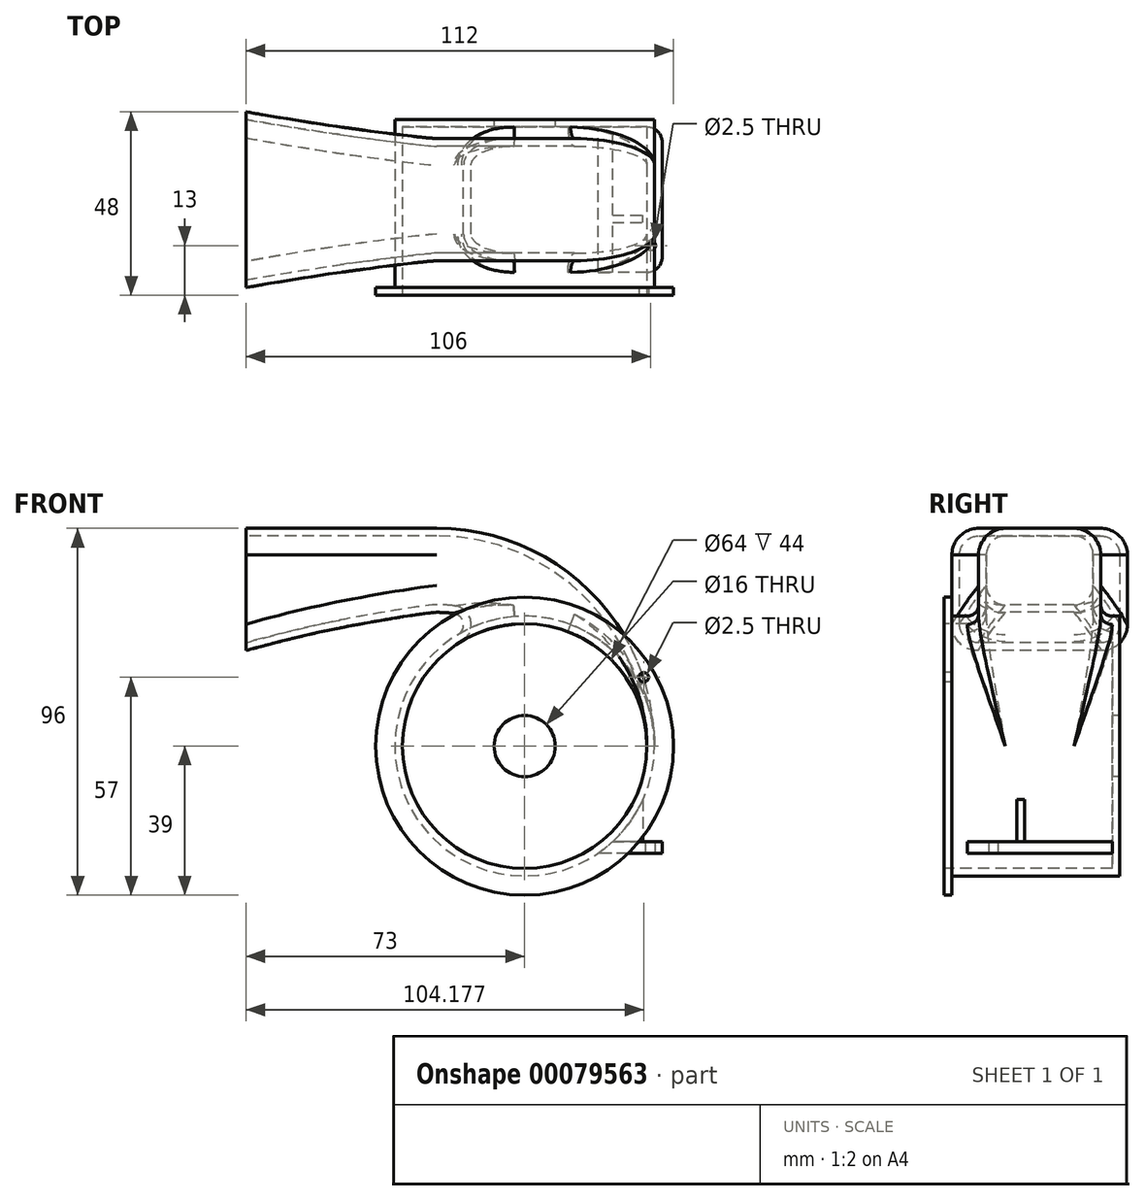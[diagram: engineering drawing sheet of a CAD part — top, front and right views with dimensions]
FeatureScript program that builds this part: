
annotation { "Feature Type Name" : "Feature", "Feature Type Description" : "" }
export const myFeature = defineFeature(function(context is Context, id is Id, definition is map)
    precondition{}
    {
        {
            var Q0;
            Q0=qCreatedBy(makeId("Front.planeOp"),FACE);
            var sketch = newSketch(context, id + "F0", { "sketchPlane" : qUnion([Q0])});
            skCircle(sketch, "E0", {"center": v(0, 0) * mm, "radius": 34 * mm});
            skSolve(sketch);
        }
        {
            var Q0;
            Q0=makeQuery(id+"F0.imprint","IMPRINT",FACE,{"disambiguationData":[TD([[makeQuery(id+"F0.imprint","IMPRINT",EDGE,{"derivedFrom":sQuery(id+"F0.wireOp",EDGE,"E0")}),1.0]])]});
            extrude(context, id + "F1", {"entities" : qUnion([Q0]), "oppositeDirection" : true, "depth" : 21 * mm, "hasSecondDirection" : true, "secondDirectionOppositeDirection" : false, "secondDirectionDepth" : 23 * mm});
        }
        {
            var Q0;
            Q0=qCreatedBy(makeId("Top.planeOp"),FACE);
            var sketch = newSketch(context, id + "F2", { "sketchPlane" : qUnion([Q0])});
            skLineSegment(sketch, "E1", {"start": v(34, 21) * mm, "end": v(34, -23) * mm});
            skLineSegment(sketch, "E2", {"start": v(-23, 15.54) * mm, "end": v(-23, -11.93) * mm, "construction": true});
            skLineSegment(sketch, "E3.bottom", {"start": v(34, 16) * mm, "end": v(12, 16) * mm});
            skLineSegment(sketch, "E3.top", {"start": v(34, -16) * mm, "end": v(12, -16) * mm});
            skLineSegment(sketch, "E3.left", {"start": v(34, 16) * mm, "end": v(34, -16) * mm});
            skLineSegment(sketch, "E3.right", {"start": v(12, 16) * mm, "end": v(12, -16) * mm});
            skPoint(sketch, "E3.middle", {"position": v(23, 0) * mm});
            skSolve(sketch);
        }
        {
            var Q0;
            Q0 = qSketchRegion(id + "F2", true);
            var Q1;
            Q1=sQuery(id+"F2.wireOp",EDGE,"E2");
            revolve(context, id + "F3", {"operationType" : NewBodyOperationType.ADD, "entities" : qUnion([Q0]), "axis" : qUnion([Q1]), "revolveType" : RevolveType.ONE_DIRECTION, "angle" : 90 * degree});
        }
        {
            var Q0;
            Q0=makeQuery(id+"F3.opRevolve","CAP_FACE",FACE,{"disambiguationData":[OSD([sQuery(id+"F2.wireOp",EDGE,"E3.bottom"),sQuery(id+"F2.wireOp",EDGE,"E3.top"),sQuery(id+"F2.wireOp",EDGE,"E3.left"),sQuery(id+"F2.wireOp",EDGE,"E3.right")])],"isStart":false});
            cPlane(context, id + "F4", {"entities" : qUnion([Q0]), "cplaneType" : CPlaneType.OFFSET, "offset" : 25 * mm, "width" : 150 * mm, "height" : 150 * mm});
        }
        {
            var Q0;
            Q0=qCreatedBy(id+"F4.planeOp",FACE);
            var sketch = newSketch(context, id + "F5", { "sketchPlane" : qUnion([Q0])});
            skLineSegment(sketch, "E4", {"start": v(-19, 57) * mm, "end": v(19, 57) * mm});
            skLineSegment(sketch, "E5", {"start": v(-19, 57) * mm, "end": v(-19, 31) * mm});
            skLineSegment(sketch, "E6", {"start": v(19, 57) * mm, "end": v(19, 31) * mm});
            skLineSegment(sketch, "E7", {"start": v(-19, 31) * mm, "end": v(19, 31) * mm});
            skSolve(sketch);
        }
        {
            var Q0;
            Q0=qCreatedBy(id+"F4.planeOp",FACE);
            cPlane(context, id + "F6", {"entities" : qUnion([Q0]), "cplaneType" : CPlaneType.OFFSET, "offset" : 25 * mm, "width" : 150 * mm, "height" : 150 * mm});
        }
        {
            var Q0;
            Q0=qCreatedBy(id+"F6.planeOp",FACE);
            var sketch = newSketch(context, id + "F7", { "sketchPlane" : qUnion([Q0])});
            skLineSegment(sketch, "E8.bottom", {"start": v(-23, 57) * mm, "end": v(23, 57) * mm});
            skLineSegment(sketch, "E8.top", {"start": v(-23, 25) * mm, "end": v(23, 25) * mm});
            skLineSegment(sketch, "E8.left", {"start": v(-23, 57) * mm, "end": v(-23, 25) * mm});
            skLineSegment(sketch, "E8.right", {"start": v(23, 57) * mm, "end": v(23, 25) * mm});
            skSolve(sketch);
        }
        {
            var Q1;
            Q1=makeQuery(id+"F3.opRevolve","CAP_FACE",FACE,{"disambiguationData":[OSD([sQuery(id+"F2.wireOp",EDGE,"E3.bottom"),sQuery(id+"F2.wireOp",EDGE,"E3.top"),sQuery(id+"F2.wireOp",EDGE,"E3.left"),sQuery(id+"F2.wireOp",EDGE,"E3.right")])],"isStart":false});
            var Q2;
            Q2=makeQuery(id+"F5.imprint","IMPRINT",FACE,{"disambiguationData":[TD([[makeQuery(id+"F5.imprint","IMPRINT",EDGE,{"derivedFrom":sQuery(id+"F5.wireOp",EDGE,"E4")}),-1.0]])]});
            var Q3;
            Q3=makeQuery(id+"F7.imprint","IMPRINT",FACE,{"disambiguationData":[TD([[makeQuery(id+"F7.imprint","IMPRINT",EDGE,{"derivedFrom":sQuery(id+"F7.wireOp",EDGE,"E8.bottom")}),-1.0]])]});
            var Q4;
            Q4=sQuery(id+"F5.wireOp",EDGE,"E7");
            var Q5;
            Q5=sQuery(id+"F5.wireOp",EDGE,"E5");
            var Q6;
            Q6=sQuery(id+"F5.wireOp",EDGE,"E4");
            var Q7;
            Q7=sQuery(id+"F5.wireOp",EDGE,"E6");
            loft(context, id + "F8", {"operationType" : NewBodyOperationType.ADD, "startCondition" : LoftEndDerivativeType.MATCH_TANGENT, "startMagnitude" : .25, "sheetProfilesArray" : [{ "sheetProfileEntities" : qUnion([Q1]) }, { "sheetProfileEntities" : qUnion([Q2]) }, { "sheetProfileEntities" : qUnion([Q3]) }], "guidesArray" : [{ "guideEntities" : qUnion([Q4]), "guideDerivativeType" : LoftGuideDerivativeType.DEFAULT, "guideDerivativeMagnitude" : 1 }, { "guideEntities" : qUnion([Q5]), "guideDerivativeType" : LoftGuideDerivativeType.DEFAULT, "guideDerivativeMagnitude" : 1 }, { "guideEntities" : qUnion([Q6]), "guideDerivativeType" : LoftGuideDerivativeType.DEFAULT, "guideDerivativeMagnitude" : 1 }, { "guideEntities" : qUnion([Q7]), "guideDerivativeType" : LoftGuideDerivativeType.DEFAULT, "guideDerivativeMagnitude" : 1 }]});
        }
        {
            var Q0;
            Q0=makeQuery(id+"F8.opLoft","SWEPT_EDGE",EDGE,{"disambiguationData":[OSD([sQuery(id+"F2.wireOp",EDGE,"E3.bottom"),sQuery(id+"F2.wireOp",EDGE,"E3.right"),sQuery(id+"F5.wireOp",EDGE,"E5"),sQuery(id+"F5.wireOp",EDGE,"E7")])]});
            var Q1;
            Q1=makeQuery(id+"F8.opLoft","SWEPT_EDGE",EDGE,{"disambiguationData":[OSD([sQuery(id+"F2.wireOp",EDGE,"E3.bottom"),sQuery(id+"F2.wireOp",EDGE,"E3.left"),sQuery(id+"F5.wireOp",EDGE,"E4"),sQuery(id+"F5.wireOp",EDGE,"E5")])]});
            var Q2;
            Q2=makeQuery(id+"F8.opLoft","SWEPT_EDGE",EDGE,{"disambiguationData":[OSD([sQuery(id+"F2.wireOp",EDGE,"E3.top"),sQuery(id+"F2.wireOp",EDGE,"E3.left"),sQuery(id+"F5.wireOp",EDGE,"E4"),sQuery(id+"F5.wireOp",EDGE,"E6")])]});
            var Q3;
            Q3=makeQuery(id+"F8.opLoft","SWEPT_EDGE",EDGE,{"disambiguationData":[OSD([sQuery(id+"F2.wireOp",EDGE,"E3.top"),sQuery(id+"F2.wireOp",EDGE,"E3.right"),sQuery(id+"F5.wireOp",EDGE,"E6"),sQuery(id+"F5.wireOp",EDGE,"E7")])]});
            fillet(context, id + "F9", {"entities" : qUnion([Q0, Q1, Q2, Q3]), "radius" : 7 * mm, "tangentPropagation" : true, "allowEdgeOverflow" : false});
        }
        {
            var Q0;
            Q0=makeQuery(id+"F3.boolean.opBoolean","INTERSECT",EDGE,{"derivedFrom":[makeQuery(id+"F1.opExtrude","SWEPT_FACE",FACE,{"disambiguationData":[OSD([sQuery(id+"F0.wireOp",EDGE,"E0")])]}),makeQuery(id+"F3.opRevolve","SWEPT_FACE",FACE,{"disambiguationData":[OSD([sQuery(id+"F2.wireOp",EDGE,"E3.top")])]})]});
            fillet(context, id + "F10", {"entities" : qUnion([Q0]), "radius" : 3 * mm, "tangentPropagation" : true, "allowEdgeOverflow" : false});
        }
        {
            var Q0;
            Q0=makeQuery(id+"F8.opLoft","CAP_FACE",FACE,{"disambiguationData":[OSD([makeQuery(id+"F7.imprint","IMPRINT",FACE,{"disambiguationData":[TD([[makeQuery(id+"F7.imprint","IMPRINT",EDGE,{"derivedFrom":sQuery(id+"F7.wireOp",EDGE,"E8.bottom")}),-1.0]])]})])],"isStart":true});
            var Q1;
            Q1=makeQuery(id+"F1.opExtrude","CAP_FACE",FACE,{"disambiguationData":[OSD([sQuery(id+"F0.wireOp",EDGE,"E0")])],"isStart":true});
            shell(context, id + "F11", {"entities" : qUnion([Q0, Q1]), "thickness" : 2 * mm});
        }
        {
            var Q0;
            {var subQ0=sQuery(id+"F0.wireOp",EDGE,"E0");Q0=makeQuery(id+"F11.opShell","OFFSET_FACE",FACE,{"disambiguationData":[OSD([subQ0]),TDD([makeQuery(id+"F1.opExtrude","CAP_FACE",FACE,{"disambiguationData":[OSD([subQ0])],"isStart":false})])]});}
            var sketch = newSketch(context, id + "F12", { "sketchPlane" : qUnion([Q0])});
            skCircle(sketch, "E9", {"center": v(0, 0) * mm, "radius": 8 * mm});
            skSolve(sketch);
        }
        {
            var Q0;
            Q0=makeQuery(id+"F12.imprint","IMPRINT",FACE,{"disambiguationData":[TD([[makeQuery(id+"F12.imprint","IMPRINT",EDGE,{"derivedFrom":sQuery(id+"F12.wireOp",EDGE,"E9")}),1.0]])]});
            extrude(context, id + "F13", {"entities" : qUnion([Q0]), "operationType" : NewBodyOperationType.REMOVE, "endBound" : BoundingType.THROUGH_ALL, "oppositeDirection" : true, "depth" : 25 * mm});
        }
        {
            var Q0;
            Q0=makeQuery(id+"F1.opExtrude","CAP_FACE",FACE,{"disambiguationData":[OSD([sQuery(id+"F0.wireOp",EDGE,"E0")])],"isStart":true});
            var sketch = newSketch(context, id + "F14", { "sketchPlane" : qUnion([Q0])});
            skCircle(sketch, "E10.0", {"center": v(0, 0) * mm, "radius": 32 * mm});
            skCircle(sketch, "E11", {"center": v(0, 0) * mm, "radius": 39 * mm});
            skSolve(sketch);
        }
        {
            var Q0;
            Q0=makeQuery(id+"F14.imprint","IMPRINT",FACE,{"disambiguationData":[TD([[makeQuery(id+"F14.imprint","IMPRINT",EDGE,{"derivedFrom":sQuery(id+"F14.wireOp",EDGE,"E11")}),1.0]])]});
            var Q1;
            Q1=makeQuery(id+"F14.imprint","IMPRINT",FACE,{"disambiguationData":[TD([[makeQuery(id+"F14.imprint","IMPRINT",EDGE,{"derivedFrom":sQuery(id+"F14.wireOp",EDGE,"E10.0")}),-1.0]])]});
            extrude(context, id + "F15", {"entities" : qUnion([Q0, Q1]), "operationType" : NewBodyOperationType.ADD, "depth" : 2 * mm});
        }
        {
            var Q0;
            Q0=qCreatedBy(makeId("Front.planeOp"),FACE);
            var sketch = newSketch(context, id + "F16", { "sketchPlane" : qUnion([Q0])});
            skLineSegment(sketch, "E12", {"start": v(0, 0) * mm, "end": v(82.23, 0) * mm, "construction": true});
            skLineSegment(sketch, "E13", {"start": v(0, 0) * mm, "end": v(0, -47.69) * mm, "construction": true});
            skCircle(sketch, "E14.0", {"center": v(0, 0) * mm, "radius": 34 * mm});
            skLineSegment(sketch, "E15", {"start": v(36, -25) * mm, "end": v(36, -28) * mm});
            skLineSegment(sketch, "E16", {"start": v(36, -28) * mm, "end": v(19.29, -28) * mm});
            skLineSegment(sketch, "E17", {"start": v(36, -25) * mm, "end": v(23.04, -25) * mm});
            skSolve(sketch);
        }
        {
            var Q0;
            Q0=makeQuery(id+"F16.imprint","IMPRINT",FACE,{"disambiguationData":[TD([[makeQuery(id+"F16.imprint","IMPRINT",EDGE,{"derivedFrom":sQuery(id+"F16.wireOp",EDGE,"E15")}),-1.0]])]});
            extrude(context, id + "F17", {"entities" : qUnion([Q0]), "operationType" : NewBodyOperationType.ADD, "depth" : 19 * mm, "hasSecondDirection" : true, "secondDirectionOppositeDirection" : true, "secondDirectionDepth" : 19 * mm});
        }
        {
            var Q0;
            Q0=makeQuery(id+"F17.opExtrude","SWEPT_FACE",FACE,{"disambiguationData":[OSD([sQuery(id+"F16.wireOp",EDGE,"E17")])]});
            var sketch = newSketch(context, id + "F18", { "sketchPlane" : qUnion([Q0])});
            skLineSegment(sketch, "E18.0", {"start": v(36, -19) * mm, "end": v(36, 19) * mm});
            skLineSegment(sketch, "E19.0", {"start": v(36, -19) * mm, "end": v(23.04, -19) * mm});
            skPoint(sketch, "E20", {"position": v(33, -12) * mm});
            skSolve(sketch);
        }
        {
            var Q0;
            Q0=sQuery(id+"F18.wireOp",VERTEX,"E20");
            var Q1;
            Q1=makeQuery(id+"F1.opExtrude","SWEPT_BODY",BODY,{"disambiguationData":[OSD([sQuery(id+"F0.wireOp",EDGE,"E0")])]});
            hole(context, id + "F19", {"style" : HoleStyle.SIMPLE, "endStyle" : HoleEndStyle.THROUGH, "holeDiameter" : 2.5 * mm, "locations" : qUnion([Q0]), "scope" : qUnion([Q1]), "isTappedThrough" : true});
        }
        {
            var Q0;
            Q0=qCreatedBy(makeId("Front.planeOp"),FACE);
            cPlane(context, id + "F20", {"entities" : qUnion([Q0]), "cplaneType" : CPlaneType.OFFSET, "offset" : 5 * mm, "width" : 150 * mm, "height" : 150 * mm});
        }
        {
            var Q0;
            Q0=qCreatedBy(id+"F20.planeOp",FACE);
            var sketch = newSketch(context, id + "F21", { "sketchPlane" : qUnion([Q0])});
            skCircle(sketch, "E21.0.0", {"center": v(0, 0) * mm, "radius": 34 * mm});
            skLineSegment(sketch, "E22.0.0", {"start": v(36, -25) * mm, "end": v(36, -28) * mm});
            skLineSegment(sketch, "E22.0.1", {"start": v(36, -28) * mm, "end": v(19.29, -28) * mm});
            skArc(sketch, "E22.0.2", {"start": v(19.29, -28) * mm, "mid": v(21.22, -26.57) * mm, "end": v(23.04, -25) * mm});
            skLineSegment(sketch, "E22.0.3", {"start": v(23.04, -25) * mm, "end": v(36, -25) * mm});
            skLineSegment(sketch, "E23", {"start": v(31, -13.96) * mm, "end": v(31, -25) * mm});
            skPoint(sketch, "E23.endSnap0", {"position": v(29.52, -25) * mm});
            skSolve(sketch);
        }
        {
            var Q0;
            {var subQ3=sQuery(id+"F21.wireOp",EDGE,"E23");Q0=makeQuery(id+"F21.imprint","IMPRINT",FACE,{"disambiguationData":[TD([[makeQuery(id+"F21.imprint","IMPRINT",EDGE,{"derivedFrom":subQ3}),-1.0]])]});}
            extrude(context, id + "F22", {"entities" : qUnion([Q0]), "operationType" : NewBodyOperationType.ADD, "depth" : 1 * mm, "hasSecondDirection" : true, "secondDirectionOppositeDirection" : true, "secondDirectionDepth" : 1 * mm});
        }
        {
            var Q0;
            Q0=makeQuery(id+"F15.opExtrude","CAP_FACE",FACE,{"disambiguationData":[OSD([sQuery(id+"F14.wireOp",EDGE,"E10.0"),sQuery(id+"F14.wireOp",EDGE,"E11")])],"isStart":false});
            var sketch = newSketch(context, id + "F23", { "sketchPlane" : qUnion([Q0])});
            skCircle(sketch, "E24", {"center": v(0, 0) * mm, "radius": 36 * mm, "construction": true});
            skPoint(sketch, "E25", {"position": v(31.18, 18) * mm});
            skLineSegment(sketch, "E26", {"start": v(31.18, 18) * mm, "end": v(0, 0) * mm, "construction": true});
            skSolve(sketch);
        }
        {
            var Q0;
            Q0=sQuery(id+"F23.wireOp",VERTEX,"E25");
            var Q1;
            Q1=makeQuery(id+"F1.opExtrude","SWEPT_BODY",BODY,{"disambiguationData":[OSD([sQuery(id+"F0.wireOp",EDGE,"E0")])]});
            hole(context, id + "F24", {"style" : HoleStyle.SIMPLE, "endStyle" : HoleEndStyle.BLIND, "holeDiameter" : 2.5 * mm, "holeDepth" : 3 * mm, "locations" : qUnion([Q0]), "scope" : qUnion([Q1])});
        }
        {
            var Q0;
            Q0=qCreatedBy(makeId("Right.planeOp"),FACE);
            var sketch = newSketch(context, id + "F25", { "sketchPlane" : qUnion([Q0])});
            skLineSegment(sketch, "E27", {"start": v(-53.31, 0) * mm, "end": v(63.47, 0) * mm, "construction": true});
            skSolve(sketch);
        }
        {
            var Q0;
            Q0=makeQuery(id+"F17.opExtrude","CAP_EDGE",EDGE,{"disambiguationData":[OSD([sQuery(id+"F16.wireOp",EDGE,"E15")])],"isStart":false});
            var Q1;
            Q1=makeQuery(id+"F17.opExtrude","CAP_EDGE",EDGE,{"disambiguationData":[OSD([sQuery(id+"F16.wireOp",EDGE,"E15")])],"isStart":true});
            fillet(context, id + "F26", {"entities" : qUnion([Q0, Q1]), "radius" : 4 * mm, "tangentPropagation" : true, "allowEdgeOverflow" : false});
        }
    });
